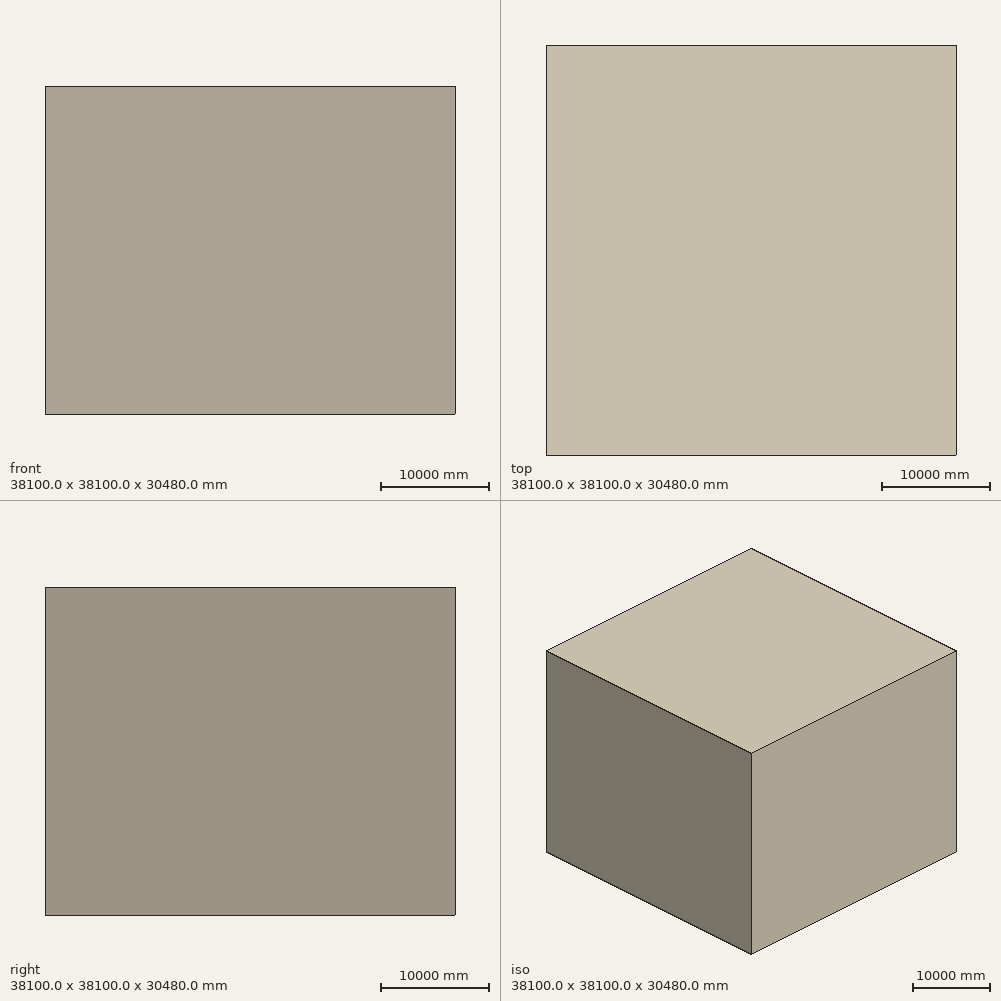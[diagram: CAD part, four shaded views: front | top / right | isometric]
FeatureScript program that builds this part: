
annotation { "Feature Type Name" : "Feature", "Feature Type Description" : "" }
export const myFeature = defineFeature(function(context is Context, id is Id, definition is map)
    precondition{}
    {
        {
            var Q0;
            Q0=qCreatedBy(makeId("Front.planeOp"),FACE);
            var sketch = newSketch(context, id + "F0", { "sketchPlane" : qUnion([Q0])});
            skLineSegment(sketch, "E0", {"start": v(0, 0) * mm, "end": v(0, 30480) * mm});
            skLineSegment(sketch, "E1", {"start": v(0, 30480) * mm, "end": v(38100, 30480) * mm});
            skLineSegment(sketch, "E2", {"start": v(38100, 30480) * mm, "end": v(38100, 0) * mm});
            skLineSegment(sketch, "E3", {"start": v(38100, 0) * mm, "end": v(0, 0) * mm});
            skSolve(sketch);
        }
        {
            var Q0;
            Q0 = qSketchRegion(id + "F0", true);
            extrude(context, id + "F1", {"entities" : qUnion([Q0]), "depth" : 38100 * mm, "offsetDistance" : 25.4 * mm});
        }
    });
